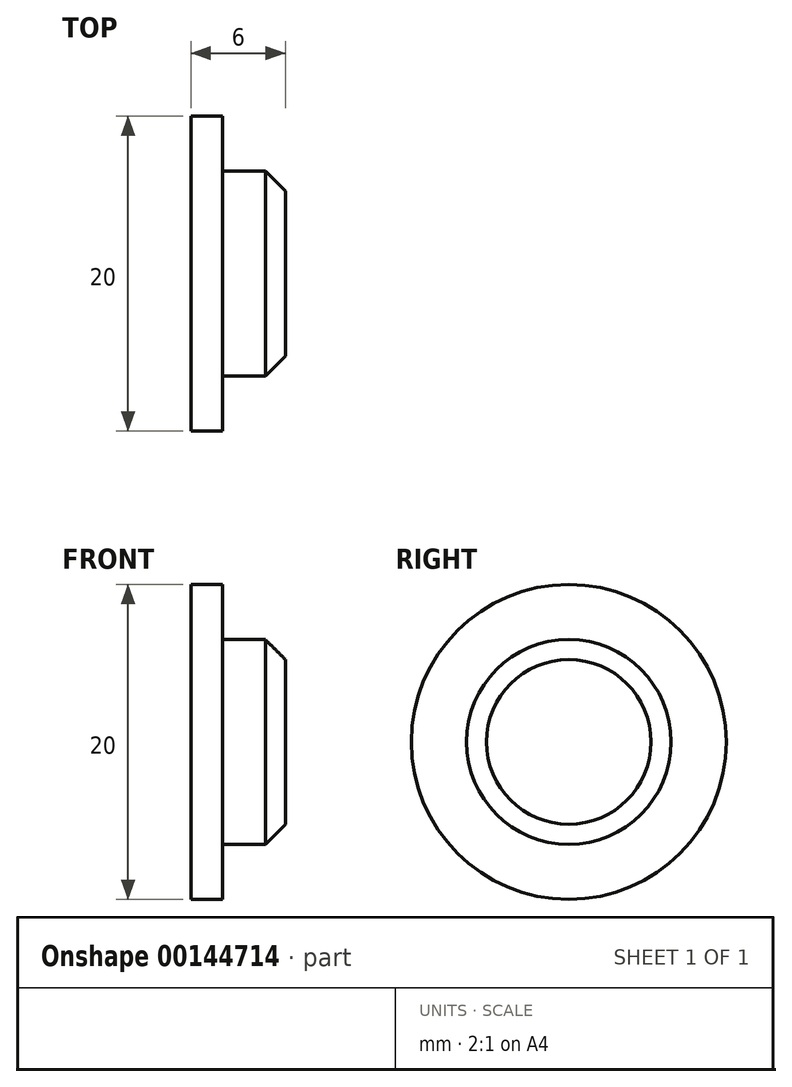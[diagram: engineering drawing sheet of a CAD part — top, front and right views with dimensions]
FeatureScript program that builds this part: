
annotation { "Feature Type Name" : "Feature", "Feature Type Description" : "" }
export const myFeature = defineFeature(function(context is Context, id is Id, definition is map)
    precondition{}
    {
        {
            var Q0;
            Q0=qCreatedBy(makeId("Front.planeOp"),FACE);
            var sketch = newSketch(context, id + "F0", { "sketchPlane" : qUnion([Q0])});
            skLineSegment(sketch, "E0", {"start": v(-4, 0) * mm, "end": v(4, 0) * mm, "construction": true});
            skLineSegment(sketch, "E1", {"start": v(0, 6.5) * mm, "end": v(4, 6.5) * mm});
            skLineSegment(sketch, "E2", {"start": v(0, 6.5) * mm, "end": v(0, 10) * mm});
            skLineSegment(sketch, "E3", {"start": v(0, 10) * mm, "end": v(-2, 10) * mm});
            skLineSegment(sketch, "E4", {"start": v(-2, 10) * mm, "end": v(-2, 0) * mm});
            skLineSegment(sketch, "E5", {"start": v(-2, 0) * mm, "end": v(4, 0) * mm});
            skLineSegment(sketch, "E6", {"start": v(4, 0) * mm, "end": v(4, 6.5) * mm});
            skSolve(sketch);
        }
        {
            var Q0;
            Q0 = qSketchRegion(id + "F0", true);
            var Q1;
            Q1=sQuery(id+"F0.wireOp",EDGE,"E0");
            revolve(context, id + "F1", {"entities" : qUnion([Q0]), "axis" : qUnion([Q1]), "revolveType" : RevolveType.FULL});
        }
        {
            var Q0;
            Q0=makeQuery(id+"F1.opRevolve","SWEPT_EDGE",EDGE,{"disambiguationData":[OSD([sQuery(id+"F0.wireOp",EDGE,"E1"),sQuery(id+"F0.wireOp",EDGE,"E6")])]});
            chamfer(context, id + "F2", {"entities" : qUnion([Q0]), "width" : 1.27 * mm, "tangentPropagation" : true});
        }
    });
